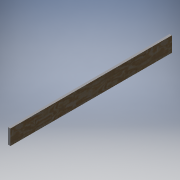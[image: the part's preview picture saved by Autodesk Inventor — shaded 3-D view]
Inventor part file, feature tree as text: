
AUTODESK INVENTOR PART (.ipt)
format: ipt  version: 2018.2 (Build 222227000, 227)  size: 103,424 bytes
history: native  units: in
note: dims shown in document units (in); Inventor stores cm internally (conversion verified against a paired STEP export)
features: extrude x1, sketch x1
ambient origin geometry x8: Origin, YZ Plane, XZ Plane, XY Plane, X Axis, Y Axis, Z Axis, Center Point
bodies: Solid1 (feature_tree)
feature tree (2):
  extrude  "Extrusion1"  [1 undecoded]
  sketch  "Sketch1"  dims[d0=0.75in d1=0.0in]
note: 1 required parameter value undecoded (feature->parameter linkage not recoverable at this tier; creation-order binding heuristic only, values carry confidence <= 0.55)
